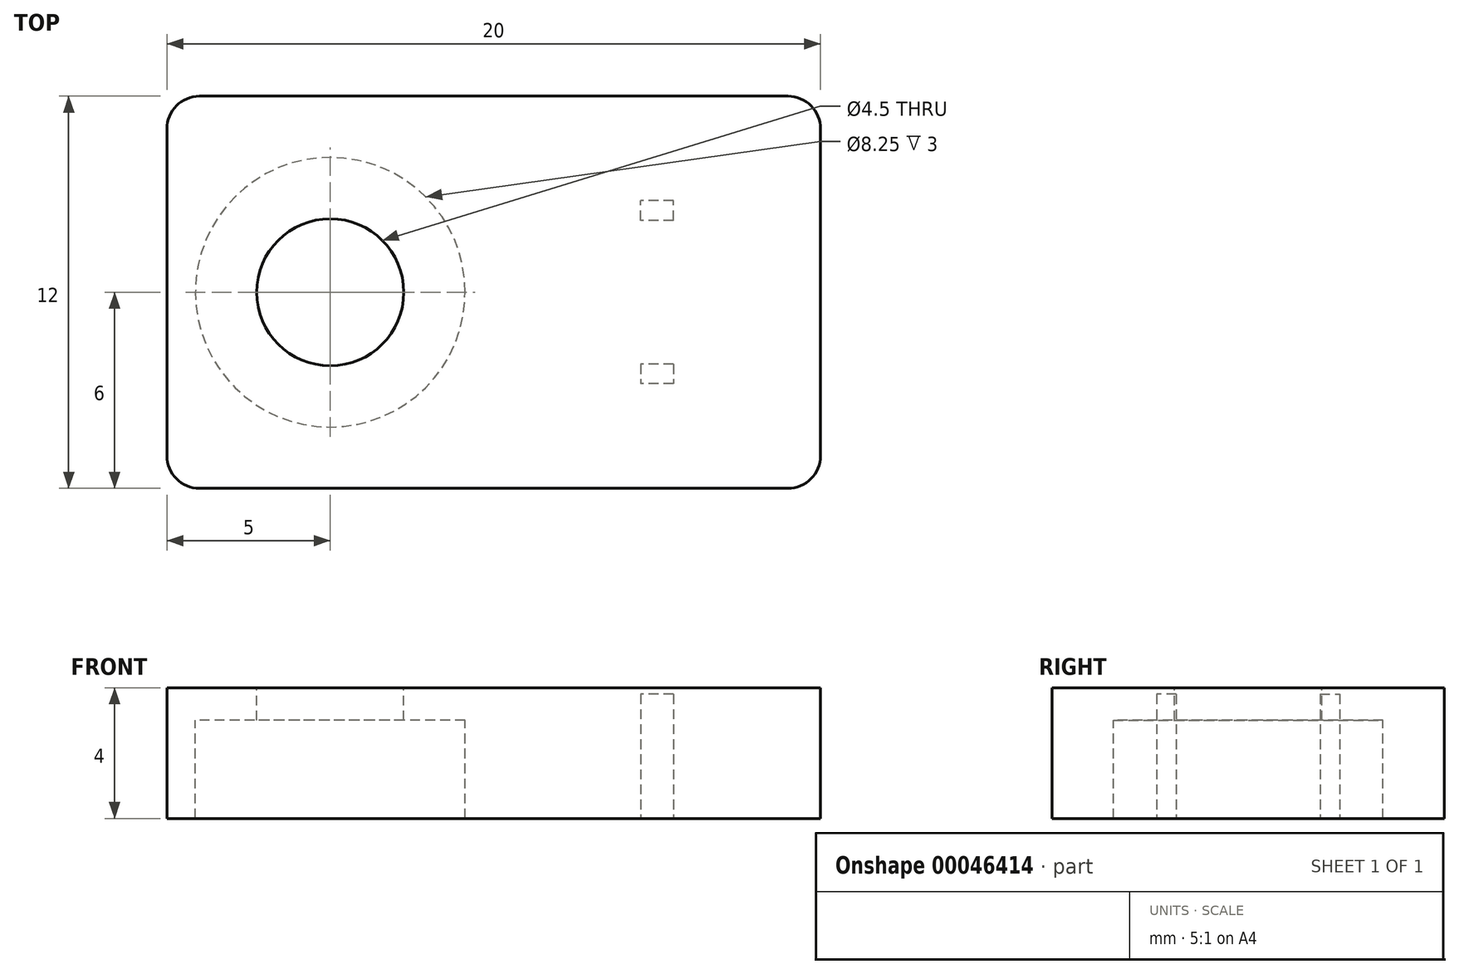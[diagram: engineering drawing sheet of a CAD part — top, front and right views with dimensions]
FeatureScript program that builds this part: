
annotation { "Feature Type Name" : "Feature", "Feature Type Description" : "" }
export const myFeature = defineFeature(function(context is Context, id is Id, definition is map)
    precondition{}
    {
        {
            var Q0;
            Q0=qCreatedBy(makeId("Top.planeOp"),FACE);
            var sketch = newSketch(context, id + "F0", { "sketchPlane" : qUnion([Q0])});
            skLineSegment(sketch, "E0.bottom", {"start": v(10, -6) * mm, "end": v(-10, -6) * mm});
            skLineSegment(sketch, "E0.top", {"start": v(10, 6) * mm, "end": v(-10, 6) * mm});
            skLineSegment(sketch, "E0.left", {"start": v(10, -6) * mm, "end": v(10, 6) * mm});
            skLineSegment(sketch, "E0.right", {"start": v(-10, -6) * mm, "end": v(-10, 6) * mm});
            skPoint(sketch, "E0.middle", {"position": v(0, 0) * mm});
            skPoint(sketch, "E1", {"position": v(-5, 0) * mm});
            skPoint(sketch, "E2", {"position": v(5, 2.5) * mm});
            skLineSegment(sketch, "E3.bottom", {"start": v(5.5, 2.2) * mm, "end": v(4.5, 2.2) * mm});
            skLineSegment(sketch, "E3.top", {"start": v(5.5, 2.8) * mm, "end": v(4.5, 2.8) * mm});
            skLineSegment(sketch, "E3.left", {"start": v(5.5, 2.2) * mm, "end": v(5.5, 2.8) * mm});
            skLineSegment(sketch, "E3.right", {"start": v(4.5, 2.2) * mm, "end": v(4.5, 2.8) * mm});
            skPoint(sketch, "E4.MirrorP", {"position": v(5, -2.5) * mm});
            skLineSegment(sketch, "E5.MirrorCS", {"start": v(5.5, -2.8) * mm, "end": v(4.5, -2.8) * mm});
            skLineSegment(sketch, "E6.MirrorCS", {"start": v(4.5, -2.2) * mm, "end": v(4.5, -2.8) * mm});
            skLineSegment(sketch, "E7.MirrorCS", {"start": v(5.5, -2.2) * mm, "end": v(4.5, -2.2) * mm});
            skLineSegment(sketch, "E8.MirrorCS", {"start": v(5.5, -2.2) * mm, "end": v(5.5, -2.8) * mm});
            skSolve(sketch);
        }
        {
            var Q0;
            Q0=makeQuery(id+"F0.imprint","IMPRINT",FACE,{"disambiguationData":[TD([[makeQuery(id+"F0.imprint","IMPRINT",EDGE,{"derivedFrom":sQuery(id+"F0.wireOp",EDGE,"E0.bottom")}),-1.0]])]});
            var Q1;
            Q1=makeQuery(id+"F0.imprint","IMPRINT",FACE,{"disambiguationData":[TD([[makeQuery(id+"F0.imprint","IMPRINT",EDGE,{"derivedFrom":sQuery(id+"F0.wireOp",EDGE,"E5.MirrorCS")}),-1.0]])]});
            var Q2;
            Q2=makeQuery(id+"F0.imprint","IMPRINT",FACE,{"disambiguationData":[TD([[makeQuery(id+"F0.imprint","IMPRINT",EDGE,{"derivedFrom":sQuery(id+"F0.wireOp",EDGE,"E3.bottom")}),-1.0]])]});
            extrude(context, id + "F1", {"entities" : qUnion([Q0, Q1, Q2]), "depth" : 4 * mm, "offsetDistance" : 25 * mm});
        }
        {
            var Q0;
            Q0=sQuery(id+"F0.wireOp",VERTEX,"E1");
            var Q1;
            Q1=makeQuery(id+"F1.opExtrude","SWEPT_BODY",BODY,{"disambiguationData":[OSD([sQuery(id+"F0.wireOp",EDGE,"E0.bottom"),sQuery(id+"F0.wireOp",EDGE,"E0.top"),sQuery(id+"F0.wireOp",EDGE,"E0.left"),sQuery(id+"F0.wireOp",EDGE,"E0.right"),sQuery(id+"F0.wireOp",EDGE,"E3.bottom"),sQuery(id+"F0.wireOp",EDGE,"E3.top"),sQuery(id+"F0.wireOp",EDGE,"E3.left"),sQuery(id+"F0.wireOp",EDGE,"E3.right"),sQuery(id+"F0.wireOp",EDGE,"E5.MirrorCS"),sQuery(id+"F0.wireOp",EDGE,"E6.MirrorCS"),sQuery(id+"F0.wireOp",EDGE,"E7.MirrorCS"),sQuery(id+"F0.wireOp",EDGE,"E8.MirrorCS")])]});
            hole(context, id + "F2", {"style" : HoleStyle.C_BORE, "endStyle" : HoleEndStyle.THROUGH, "oppositeDirection" : true, "holeDiameter" : 4.5 * mm, "cBoreDiameter" : 8.25 * mm, "cBoreDepth" : 3 * mm, "majorDiameter" : 5 * mm, "isTappedThrough" : true, "tappedDepth" : 4 * mm, "tapClearance" : 3, "locations" : qUnion([Q0]), "scope" : qUnion([Q1]), "startStyle" : HoleStartStyle.PART});
        }
        {
            var Q0;
            Q0=makeQuery(id+"F1.opExtrude","SWEPT_EDGE",EDGE,{"disambiguationData":[OSD([sQuery(id+"F0.wireOp",EDGE,"E0.top"),sQuery(id+"F0.wireOp",EDGE,"E0.right")])]});
            var Q1;
            Q1=makeQuery(id+"F1.opExtrude","SWEPT_EDGE",EDGE,{"disambiguationData":[OSD([sQuery(id+"F0.wireOp",EDGE,"E0.top"),sQuery(id+"F0.wireOp",EDGE,"E0.left")])]});
            var Q2;
            Q2=makeQuery(id+"F1.opExtrude","SWEPT_EDGE",EDGE,{"disambiguationData":[OSD([sQuery(id+"F0.wireOp",EDGE,"E0.bottom"),sQuery(id+"F0.wireOp",EDGE,"E0.right")])]});
            var Q3;
            Q3=makeQuery(id+"F1.opExtrude","SWEPT_EDGE",EDGE,{"disambiguationData":[OSD([sQuery(id+"F0.wireOp",EDGE,"E0.bottom"),sQuery(id+"F0.wireOp",EDGE,"E0.left")])]});
            fillet(context, id + "F3", {"entities" : qUnion([Q0, Q1, Q2, Q3]), "tangentPropagation" : true, "radius" : 1 * mm, "defaultsChanged" : false, "vertexSettings" : [], "allowEdgeOverflow" : false});
        }
        {
            var Q0;
            Q0=makeQuery(id+"F0.imprint","IMPRINT",FACE,{"disambiguationData":[TD([[makeQuery(id+"F0.imprint","IMPRINT",EDGE,{"derivedFrom":sQuery(id+"F0.wireOp",EDGE,"E5.MirrorCS")}),-1.0]])]});
            var Q1;
            Q1=makeQuery(id+"F0.imprint","IMPRINT",FACE,{"disambiguationData":[TD([[makeQuery(id+"F0.imprint","IMPRINT",EDGE,{"derivedFrom":sQuery(id+"F0.wireOp",EDGE,"E3.bottom")}),-1.0]])]});
            extrude(context, id + "F4", {"entities" : qUnion([Q0, Q1]), "operationType" : NewBodyOperationType.REMOVE, "depth" : 3.8 * mm, "offsetDistance" : 25 * mm});
        }
    });
